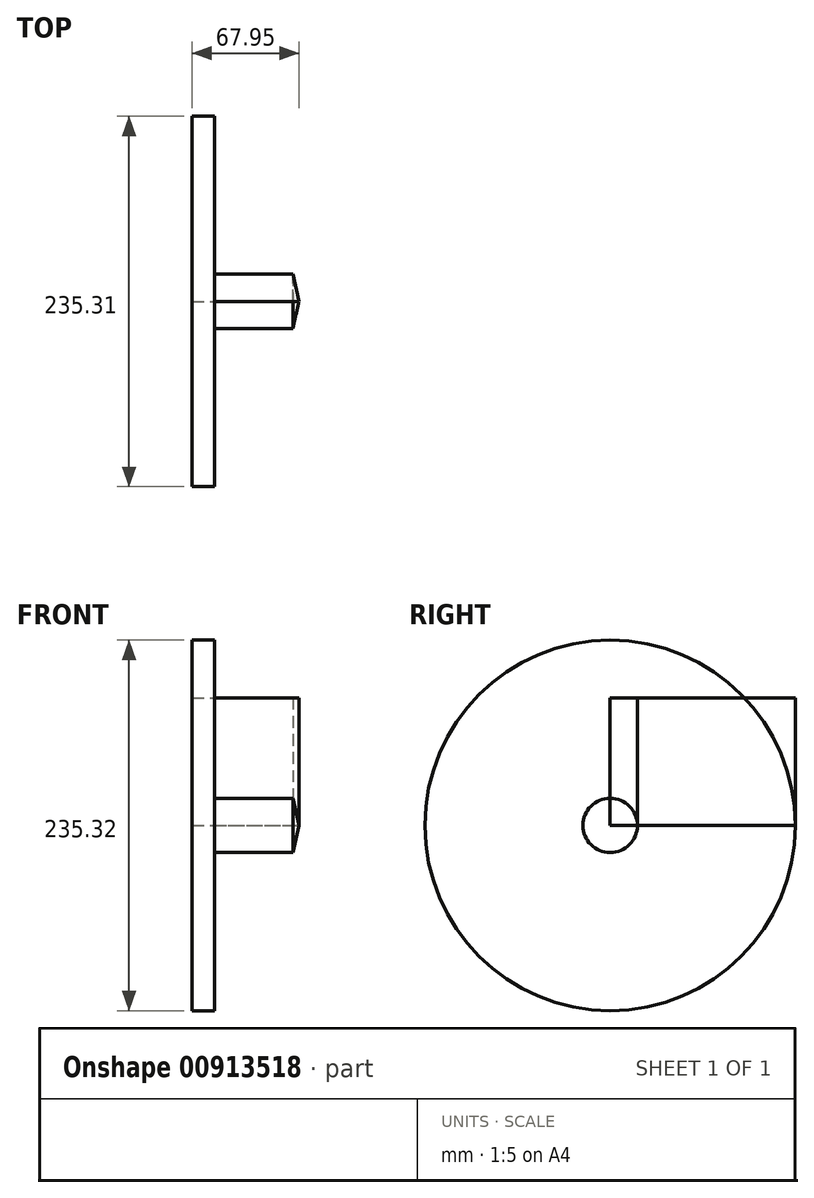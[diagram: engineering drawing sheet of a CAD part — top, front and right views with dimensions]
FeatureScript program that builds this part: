
annotation { "Feature Type Name" : "Feature", "Feature Type Description" : "" }
export const myFeature = defineFeature(function(context is Context, id is Id, definition is map)
    precondition{}
    {
        {
            var Q0;
            Q0=qCreatedBy(makeId("Top.planeOp"),FACE);
            var sketch = newSketch(context, id + "F0", { "sketchPlane" : qUnion([Q0])});
            skLineSegment(sketch, "E0", {"start": v(-56.1, 62.8) * mm, "end": v(-56.1, -54.85) * mm});
            skLineSegment(sketch, "E1", {"start": v(-56.1, -54.85) * mm, "end": v(11.85, -54.85) * mm});
            skLineSegment(sketch, "E2", {"start": v(-56.1, 62.8) * mm, "end": v(-41.76, 62.8) * mm});
            skLineSegment(sketch, "E3", {"start": v(-41.76, 62.8) * mm, "end": v(-41.76, -37.58) * mm});
            skLineSegment(sketch, "E4", {"start": v(-41.76, -37.58) * mm, "end": v(7.91, -37.58) * mm});
            skLineSegment(sketch, "E5", {"start": v(7.91, -37.58) * mm, "end": v(11.85, -54.85) * mm});
            skSolve(sketch);
        }
        {
            var Q0;
            Q0=makeQuery(id+"F0.imprint","IMPRINT",FACE,{"disambiguationData":[TD([[makeQuery(id+"F0.imprint","IMPRINT",EDGE,{"derivedFrom":sQuery(id+"F0.wireOp",EDGE,"E0")}),1.0]])]});
            extrude(context, id + "F1", {"entities" : qUnion([Q0]), "depth" : 81.03 * mm, "offsetDistance" : 25.4 * mm});
        }
        {
            var Q0;
            Q0=makeQuery(id+"F0.imprint","IMPRINT",FACE,{"disambiguationData":[TD([[makeQuery(id+"F0.imprint","IMPRINT",EDGE,{"derivedFrom":sQuery(id+"F0.wireOp",EDGE,"E0")}),1.0]])]});
            var Q1;
            Q1=sQuery(id+"F0.wireOp",EDGE,"E1");
            revolve(context, id + "F2", {"surfaceOperationType" : NewSurfaceOperationType.NEW, "entities" : qUnion([Q0]), "axis" : qUnion([Q1]), "revolveType" : RevolveType.FULL});
        }
    });
